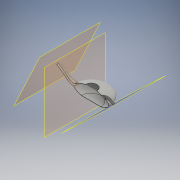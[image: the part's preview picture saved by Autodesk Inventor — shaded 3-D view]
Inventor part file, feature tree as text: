
AUTODESK INVENTOR PART (.ipt)
format: ipt  version: 2016 (Build 200138000, 138)  size: 526,336 bytes
history: native  units: in
note: dims shown in document units (in); Inventor stores cm internally (conversion verified against a paired STEP export)
features: delete_face x7, sketch x6, plane x3, other x2, surface_op x2, revolve x1, loft x1, shell x1, sweep x1
ambient origin geometry x8: Origin, YZ Plane, XZ Plane, XY Plane, X Axis, Y Axis, Z Axis, Center Point
bodies: Solid1 (feature_tree)
feature tree (24):
  other  "CrossSection1"
  revolve  "Revolution1"  [1 undecoded]
  sketch  "Sketch2"  dims[d9=0.0in d10=90.0deg d11=0.0in d12=90.0deg d13=0.0in d14=90.0deg]
  plane  "Work Plane1"
  sketch  "Sketch4"  dims[d20=0.1969in]
  plane  "Work Plane2"
  plane  "Work Plane3"
  loft  "Loft2"
  shell  "Shell1"  Thickness=0.0in
  sweep  "Sweep1"
  delete_face  "Delete Face1"
  delete_face  "Delete Face2"
  surface_op  "Stitch Surface1"
  delete_face  "Delete Face3"
  delete_face  "Delete Face4"
  delete_face  "Delete Face5"
  delete_face  "Delete Face6"
  delete_face  "Delete Face7"
  sketch  "Sketch1"  dims[d0=90.0deg d1=0.0in d2=0.0in]
  sketch  "Sketch3"  dims[d15=0.005in d16=0.013in d17=0.5in d18=0.0in d19=2.0in]
  sketch  "Sketch10"  dims[d21=0.0in]
  sketch  "Sketch11"
  other  "Srf1"
  surface_op  "Boundary Patch1"
note: 1 required parameter value undecoded (feature->parameter linkage not recoverable at this tier; creation-order binding heuristic only, values carry confidence <= 0.55)
